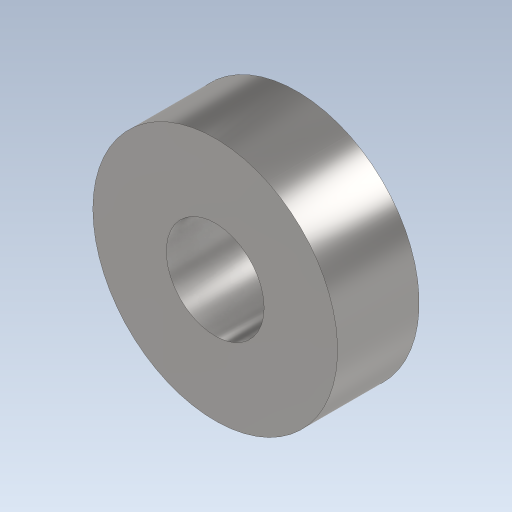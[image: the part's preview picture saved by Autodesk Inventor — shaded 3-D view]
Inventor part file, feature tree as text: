
AUTODESK INVENTOR PART (.ipt)
format: ipt  version: 2023 (Build 270158000, 158)  size: 124,928 bytes
history: native  units: mm
features: extrude x2, sketch x2, other x1, projected_geometry x1
ambient origin geometry x8: Origin, YZ Plane, XZ Plane, XY Plane, X Axis, Y Axis, Z Axis, Center Point
bodies: Body1 (feature_tree)
feature tree (6):
  other  "솔리드1"
  extrude  "돌출1"  Depth=17.0mm
  extrude  "돌출2"  Depth=6.0mm
  sketch  "스케치1"
  sketch  "스케치2"
  projected_geometry  "투영된 루프1"
